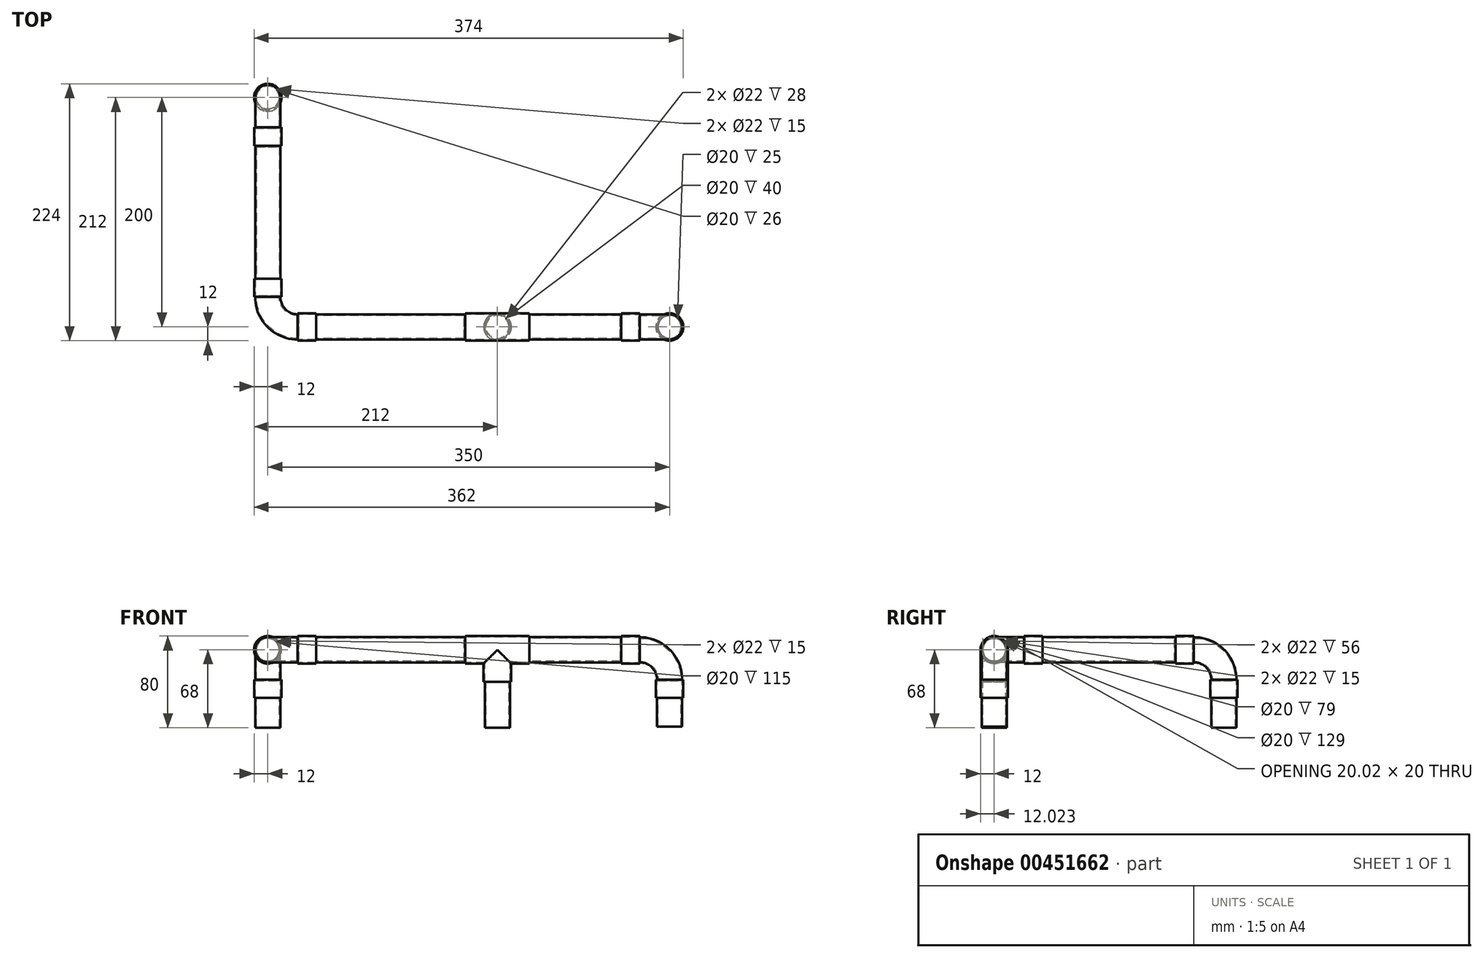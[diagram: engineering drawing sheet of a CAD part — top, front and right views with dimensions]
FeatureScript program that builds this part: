
annotation { "Feature Type Name" : "Feature", "Feature Type Description" : "" }
export const myFeature = defineFeature(function(context is Context, id is Id, definition is map)
    precondition{}
    {
        {
            var Q0;
            Q0=qCreatedBy(makeId("Top.planeOp"),FACE);
            var sketch = newSketch(context, id + "F0", { "sketchPlane" : qUnion([Q0])});
            skLineSegment(sketch, "E0", {"start": v(0, 26) * mm, "end": v(0, 26) * mm});
            skLineSegment(sketch, "E1", {"start": v(26, 0) * mm, "end": v(26, 0) * mm});
            skPoint(sketch, "E2.visualSharp", {"position": v(0, 0) * mm});
            skArc(sketch, "E2.filletArc", {"start": v(0, 26) * mm, "mid": v(7.62, 7.62) * mm, "end": v(26, 0) * mm});
            skPoint(sketch, "E3", {"position": v(0, 26) * mm});
            skPoint(sketch, "E4", {"position": v(26, 0) * mm});
            skSolve(sketch);
        }
        {
            var Q0;
            Q0=qCreatedBy(makeId("Front.planeOp"),FACE);
            var Q1;
            Q1=sQuery(id+"F0.wireOp",VERTEX,"E3");
            cPlane(context, id + "F1", {"entities" : qUnion([Q0, Q1]), "cplaneType" : CPlaneType.PLANE_POINT, "offset" : 25 * mm, "width" : 150 * mm, "height" : 150 * mm});
        }
        {
            var Q0;
            Q0=qCreatedBy(id+"F1.planeOp",FACE);
            var sketch = newSketch(context, id + "F2", { "sketchPlane" : qUnion([Q0])});
            skCircle(sketch, "E5", {"center": v(0, 0) * mm, "radius": 11 * mm});
            skSolve(sketch);
        }
        {
            var Q0;
            Q0=makeQuery(id+"F2.imprint","IMPRINT",FACE,{"disambiguationData":[TD([[makeQuery(id+"F2.imprint","IMPRINT",EDGE,{"derivedFrom":sQuery(id+"F2.wireOp",EDGE,"E5")}),1.0]])]});
            var Q1;
            Q1=sQuery(id+"F0.wireOp",EDGE,"E2.filletArc");
            sweep(context, id + "F3", {"profiles" : qUnion([Q0]), "path" : qUnion([Q1])});
        }
        {
            var Q0;
            Q0=makeQuery(id+"F3.opSweep","CAP_FACE",FACE,{"disambiguationData":[OSD([sQuery(id+"F0.wireOp",VERTEX,"E2.filletArc.start"),sQuery(id+"F2.wireOp",EDGE,"E5")])],"isStart":true});
            var sketch = newSketch(context, id + "F4", { "sketchPlane" : qUnion([Q0])});
            skCircle(sketch, "E6", {"center": v(0, 0) * mm, "radius": 12 * mm});
            skSolve(sketch);
        }
        {
            var Q0;
            Q0=makeQuery(id+"F4.imprint","IMPRINT",FACE,{"disambiguationData":[TD([[makeQuery(id+"F4.imprint","IMPRINT",EDGE,{"derivedFrom":sQuery(id+"F4.wireOp",EDGE,"E6")}),1.0]])]});
            var Q1;
            Q1=makeQuery(id+"F4.imprint","IMPRINT",FACE,{"disambiguationData":[TD([[makeQuery(id+"F4.imprint","IMPRINT",EDGE,{"derivedFrom":makeQuery(id+"F3.opSweep","CAP_EDGE",EDGE,{"disambiguationData":[OSD([sQuery(id+"F0.wireOp",VERTEX,"E2.filletArc.start"),sQuery(id+"F2.wireOp",EDGE,"E5")])],"isStart":true})}),-1.0]])]});
            extrude(context, id + "F5", {"entities" : qUnion([Q0, Q1]), "operationType" : NewBodyOperationType.ADD, "depth" : 16 * mm});
        }
        {
            var Q0;
            Q0=makeQuery(id+"F3.opSweep","CAP_FACE",FACE,{"disambiguationData":[OSD([sQuery(id+"F0.wireOp",VERTEX,"E2.filletArc.end"),sQuery(id+"F2.wireOp",EDGE,"E5")])],"isStart":false});
            var sketch = newSketch(context, id + "F6", { "sketchPlane" : qUnion([Q0])});
            skCircle(sketch, "E7", {"center": v(0, 0) * mm, "radius": 12 * mm});
            skSolve(sketch);
        }
        {
            var Q0;
            Q0=makeQuery(id+"F6.imprint","IMPRINT",FACE,{"disambiguationData":[TD([[makeQuery(id+"F6.imprint","IMPRINT",EDGE,{"derivedFrom":makeQuery(id+"F3.opSweep","CAP_EDGE",EDGE,{"disambiguationData":[OSD([sQuery(id+"F0.wireOp",VERTEX,"E2.filletArc.end"),sQuery(id+"F2.wireOp",EDGE,"E5")])],"isStart":false})}),1.0]])]});
            var Q1;
            Q1=makeQuery(id+"F6.imprint","IMPRINT",FACE,{"disambiguationData":[TD([[makeQuery(id+"F6.imprint","IMPRINT",EDGE,{"derivedFrom":sQuery(id+"F6.wireOp",EDGE,"E7")}),1.0]])]});
            extrude(context, id + "F7", {"entities" : qUnion([Q0, Q1]), "operationType" : NewBodyOperationType.ADD, "depth" : 16 * mm});
        }
        {
            var Q0;
            Q0=makeQuery(id+"F3.opSweep","SWEPT_BODY",BODY,{"disambiguationData":[OSD([sQuery(id+"F0.wireOp",EDGE,"E2.filletArc"),sQuery(id+"F2.wireOp",EDGE,"E5")])]});
            transform(context, id + "F8", {"entities" : qUnion([Q0]), "transformType" : TransformType.TRANSLATION_3D, "dx" : 350 * mm, "dy" : 0 * mm, "dz" : 0 * mm, "makeCopy" : true});
        }
        {
            var Q0;
            Q0=qCreatedBy(makeId("Top.planeOp"),FACE);
            var sketch = newSketch(context, id + "F9", { "sketchPlane" : qUnion([Q0])});
            skLineSegment(sketch, "E8.0", {"start": v(338, 42) * mm, "end": v(362, 42) * mm});
            skLineSegment(sketch, "E9", {"start": v(350, 42) * mm, "end": v(350, 75.2) * mm});
            skSolve(sketch);
        }
        {
            var Q0;
            Q0=makeQuery(id+"F8.opPattern","COPY",BODY,{"derivedFrom":makeQuery(id+"F3.opSweep","SWEPT_BODY",BODY,{"disambiguationData":[OSD([sQuery(id+"F0.wireOp",EDGE,"E2.filletArc"),sQuery(id+"F2.wireOp",EDGE,"E5")])]}),"instanceName":"1"});
            var Q1;
            Q1=sQuery(id+"F9.wireOp",EDGE,"E9");
            transform(context, id + "F10", {"entities" : qUnion([Q0]), "transformType" : TransformType.ROTATION, "transformAxis" : qUnion([Q1]), "angle" : 180 * degree, "makeCopy" : false});
        }
        {
            var Q0;
            Q0=qCreatedBy(makeId("Top.planeOp"),FACE);
            var sketch = newSketch(context, id + "F11", { "sketchPlane" : qUnion([Q0])});
            skLineSegment(sketch, "E10", {"start": v(0, 0) * mm, "end": v(0, 200) * mm});
            skLineSegment(sketch, "E11", {"start": v(0, 0) * mm, "end": v(200, 0) * mm});
            skLineSegment(sketch, "E12", {"start": v(200, 0) * mm, "end": v(350, 0) * mm});
            skLineSegment(sketch, "E13", {"start": v(350, 0) * mm, "end": v(350, 70) * mm});
            skSolve(sketch);
        }
        {
            var Q0;
            Q0=qCreatedBy(makeId("Front.planeOp"),FACE);
            var sketch = newSketch(context, id + "F12", { "sketchPlane" : qUnion([Q0])});
            skPoint(sketch, "E14.0", {"position": v(200, 0) * mm});
            skLineSegment(sketch, "E15", {"start": v(200, 0) * mm, "end": v(200, -70) * mm});
            skSolve(sketch);
        }
        {
            var Q0;
            Q0=qCreatedBy(makeId("Front.planeOp"),FACE);
            var Q1;
            Q1=sQuery(id+"F11.wireOp",VERTEX,"E10.end");
            cPlane(context, id + "F13", {"entities" : qUnion([Q0, Q1]), "cplaneType" : CPlaneType.PLANE_POINT, "offset" : 25 * mm, "width" : 150 * mm, "height" : 150 * mm});
        }
        {
            var Q0;
            Q0=qCreatedBy(id+"F13.planeOp",FACE);
            var sketch = newSketch(context, id + "F14", { "sketchPlane" : qUnion([Q0])});
            skLineSegment(sketch, "E16", {"start": v(0, 0) * mm, "end": v(0, -70) * mm});
            skSolve(sketch);
        }
        {
            var Q0;
            Q0=makeQuery(id+"F3.opSweep","SWEPT_BODY",BODY,{"disambiguationData":[OSD([sQuery(id+"F0.wireOp",EDGE,"E2.filletArc"),sQuery(id+"F2.wireOp",EDGE,"E5")])]});
            var Q1;
            Q1=sQuery(id+"F0.wireOp",VERTEX,"E2.visualSharp");
            var Q2;
            Q2=sQuery(id+"F14.wireOp",VERTEX,"E16.start");
            transform(context, id + "F15", {"entities" : qUnion([Q0]), "transformType" : TransformType.TRANSLATION_ENTITY, "oppositeDirectionEntity" : false, "transformLine" : qUnion([Q1, Q2]), "makeCopy" : true});
        }
        {
            var Q0;
            Q0=makeQuery(id+"F15.opPattern","COPY",BODY,{"derivedFrom":makeQuery(id+"F3.opSweep","SWEPT_BODY",BODY,{"disambiguationData":[OSD([sQuery(id+"F0.wireOp",EDGE,"E2.filletArc"),sQuery(id+"F2.wireOp",EDGE,"E5")])]}),"instanceName":"1"});
            var Q1;
            Q1=sQuery(id+"F14.wireOp",EDGE,"E16");
            transform(context, id + "F16", {"entities" : qUnion([Q0]), "transformType" : TransformType.ROTATION, "transformAxis" : qUnion([Q1]), "angle" : 90 * degree, "makeCopy" : false});
        }
        {
            var Q0;
            Q0=makeQuery(id+"F15.opPattern","COPY",BODY,{"derivedFrom":makeQuery(id+"F3.opSweep","SWEPT_BODY",BODY,{"disambiguationData":[OSD([sQuery(id+"F0.wireOp",EDGE,"E2.filletArc"),sQuery(id+"F2.wireOp",EDGE,"E5")])]}),"instanceName":"1"});
            var Q1;
            Q1=sQuery(id+"F11.wireOp",EDGE,"E10");
            transform(context, id + "F17", {"entities" : qUnion([Q0]), "transformType" : TransformType.ROTATION, "transformAxis" : qUnion([Q1]), "angle" : 90 * degree, "makeCopy" : false});
        }
        {
            var Q0;
            Q0=makeQuery(id+"F5.opExtrude","CAP_FACE",FACE,{"disambiguationData":[OSD([sQuery(id+"F4.wireOp",EDGE,"E6")])],"isStart":false});
            var sketch = newSketch(context, id + "F18", { "sketchPlane" : qUnion([Q0])});
            skCircle(sketch, "E17", {"center": v(0, 0) * mm, "radius": 11 * mm});
            skSolve(sketch);
        }
        {
            var Q0;
            Q0=makeQuery(id+"F18.imprint","IMPRINT",FACE,{"disambiguationData":[TD([[makeQuery(id+"F18.imprint","IMPRINT",EDGE,{"derivedFrom":sQuery(id+"F18.wireOp",EDGE,"E17")}),1.0]])]});
            extrude(context, id + "F19", {"entities" : qUnion([Q0]), "endBound" : BoundingType.UP_TO_NEXT, "depth" : 25 * mm});
        }
        {
            var Q0;
            Q0=qCreatedBy(makeId("Right.planeOp"),FACE);
            var Q1;
            Q1=sQuery(id+"F12.wireOp",VERTEX,"E14.0");
            cPlane(context, id + "F20", {"entities" : qUnion([Q0, Q1]), "cplaneType" : CPlaneType.PLANE_POINT, "offset" : 25 * mm, "width" : 150 * mm, "height" : 150 * mm});
        }
        {
            var Q0;
            Q0=qCreatedBy(id+"F20.planeOp",FACE);
            var sketch = newSketch(context, id + "F21", { "sketchPlane" : qUnion([Q0])});
            skCircle(sketch, "E18", {"center": v(0, 0) * mm, "radius": 12 * mm});
            skSolve(sketch);
        }
        {
            var Q0;
            Q0=makeQuery(id+"F21.imprint","IMPRINT",FACE,{"disambiguationData":[TD([[makeQuery(id+"F21.imprint","IMPRINT",EDGE,{"derivedFrom":sQuery(id+"F21.wireOp",EDGE,"E18")}),1.0]])]});
            extrude(context, id + "F22", {"entities" : qUnion([Q0]), "depth" : 56 * mm, "symmetric" : true});
        }
        {
            var Q0;
            Q0=qCreatedBy(makeId("Top.planeOp"),FACE);
            var sketch = newSketch(context, id + "F23", { "sketchPlane" : qUnion([Q0])});
            skPoint(sketch, "E19.0", {"position": v(200, 0) * mm});
            skCircle(sketch, "E20", {"center": v(200, 0) * mm, "radius": 12 * mm});
            skSolve(sketch);
        }
        {
            var Q0;
            Q0 = qSketchRegion(id + "F23", true);
            extrude(context, id + "F24", {"entities" : qUnion([Q0]), "operationType" : NewBodyOperationType.ADD, "oppositeDirection" : true, "depth" : 28 * mm});
        }
        {
            var Q0;
            Q0=makeQuery(id+"F7.opExtrude","CAP_FACE",FACE,{"disambiguationData":[OSD([sQuery(id+"F6.wireOp",EDGE,"E7")])],"isStart":false});
            var sketch = newSketch(context, id + "F25", { "sketchPlane" : qUnion([Q0])});
            skCircle(sketch, "E21", {"center": v(0, 0) * mm, "radius": 11 * mm});
            skSolve(sketch);
        }
        {
            var Q0;
            Q0=makeQuery(id+"F25.imprint","IMPRINT",FACE,{"disambiguationData":[TD([[makeQuery(id+"F25.imprint","IMPRINT",EDGE,{"derivedFrom":sQuery(id+"F25.wireOp",EDGE,"E21")}),1.0]])]});
            extrude(context, id + "F26", {"entities" : qUnion([Q0]), "endBound" : BoundingType.UP_TO_NEXT, "depth" : 25 * mm});
        }
        {
            var Q0;
            Q0=makeQuery(id+"F22.opExtrude","CAP_FACE",FACE,{"disambiguationData":[OSD([sQuery(id+"F21.wireOp",EDGE,"E18")])],"isStart":false});
            var sketch = newSketch(context, id + "F27", { "sketchPlane" : qUnion([Q0])});
            skCircle(sketch, "E22", {"center": v(0, 0) * mm, "radius": 11 * mm});
            skSolve(sketch);
        }
        {
            var Q0;
            Q0 = qSketchRegion(id + "F27", true);
            extrude(context, id + "F28", {"entities" : qUnion([Q0]), "endBound" : BoundingType.UP_TO_NEXT, "depth" : 25 * mm});
        }
        {
            var Q0;
            Q0=makeQuery(id+"F8.opPattern","COPY",BODY,{"derivedFrom":makeQuery(id+"F3.opSweep","SWEPT_BODY",BODY,{"disambiguationData":[OSD([sQuery(id+"F0.wireOp",EDGE,"E2.filletArc"),sQuery(id+"F2.wireOp",EDGE,"E5")])]}),"instanceName":"1"});
            var Q1;
            Q1=sQuery(id+"F11.wireOp",EDGE,"E12");
            transform(context, id + "F29", {"entities" : qUnion([Q0]), "transformType" : TransformType.ROTATION, "transformAxis" : qUnion([Q1]), "angle" : 270 * degree, "makeCopy" : false});
        }
        {
            var Q0;
            Q0=makeQuery(id+"F24.opExtrude","CAP_FACE",FACE,{"disambiguationData":[OSD([sQuery(id+"F23.wireOp",EDGE,"E20")])],"isStart":false});
            var sketch = newSketch(context, id + "F30", { "sketchPlane" : qUnion([Q0])});
            skCircle(sketch, "E23", {"center": v(200, 0) * mm, "radius": 11 * mm});
            skSolve(sketch);
        }
        {
            var Q0;
            Q0=makeQuery(id+"F30.imprint","IMPRINT",FACE,{"disambiguationData":[TD([[makeQuery(id+"F30.imprint","IMPRINT",EDGE,{"derivedFrom":sQuery(id+"F30.wireOp",EDGE,"E23")}),1.0]])]});
            extrude(context, id + "F31", {"entities" : qUnion([Q0]), "depth" : 40 * mm});
        }
        {
            var Q0;
            Q0=makeQuery(id+"F8.opPattern","COPY",FACE,{"derivedFrom":makeQuery(id+"F5.opExtrude","CAP_FACE",FACE,{"disambiguationData":[OSD([sQuery(id+"F4.wireOp",EDGE,"E6")])],"isStart":false}),"instanceName":"1"});
            var sketch = newSketch(context, id + "F32", { "sketchPlane" : qUnion([Q0])});
            skCircle(sketch, "E24", {"center": v(350, 0) * mm, "radius": 11 * mm});
            skSolve(sketch);
        }
        {
            var Q0;
            Q0=makeQuery(id+"F32.imprint","IMPRINT",FACE,{"disambiguationData":[TD([[makeQuery(id+"F32.imprint","IMPRINT",EDGE,{"derivedFrom":sQuery(id+"F32.wireOp",EDGE,"E24")}),1.0]])]});
            extrude(context, id + "F33", {"entities" : qUnion([Q0]), "depth" : 25 * mm});
        }
        {
            var Q0;
            Q0=makeQuery(id+"F15.opPattern","COPY",FACE,{"derivedFrom":makeQuery(id+"F5.opExtrude","CAP_FACE",FACE,{"disambiguationData":[OSD([sQuery(id+"F4.wireOp",EDGE,"E6")])],"isStart":false}),"instanceName":"1"});
            var sketch = newSketch(context, id + "F34", { "sketchPlane" : qUnion([Q0])});
            skCircle(sketch, "E25", {"center": v(0, -200) * mm, "radius": 11 * mm});
            skSolve(sketch);
        }
        {
            var Q0;
            Q0=makeQuery(id+"F34.imprint","IMPRINT",FACE,{"disambiguationData":[TD([[makeQuery(id+"F34.imprint","IMPRINT",EDGE,{"derivedFrom":sQuery(id+"F34.wireOp",EDGE,"E25")}),1.0]])]});
            extrude(context, id + "F35", {"entities" : qUnion([Q0]), "depth" : 26 * mm});
        }
        {
            var Q0;
            Q0=makeQuery(id+"F7.opExtrude","CAP_FACE",FACE,{"disambiguationData":[OSD([sQuery(id+"F6.wireOp",EDGE,"E7")])],"isStart":false});
            var Q1;
            Q1=makeQuery(id+"F5.opExtrude","CAP_FACE",FACE,{"disambiguationData":[OSD([sQuery(id+"F4.wireOp",EDGE,"E6")])],"isStart":false});
            shell(context, id + "F36", {"entities" : qUnion([Q0, Q1]), "thickness" : 1 * mm});
        }
        {
            var Q0;
            Q0=makeQuery(id+"F8.opPattern","COPY",FACE,{"derivedFrom":makeQuery(id+"F5.opExtrude","CAP_FACE",FACE,{"disambiguationData":[OSD([sQuery(id+"F4.wireOp",EDGE,"E6")])],"isStart":false}),"instanceName":"1"});
            var Q1;
            Q1=makeQuery(id+"F8.opPattern","COPY",FACE,{"derivedFrom":makeQuery(id+"F7.opExtrude","CAP_FACE",FACE,{"disambiguationData":[OSD([sQuery(id+"F6.wireOp",EDGE,"E7")])],"isStart":false}),"instanceName":"1"});
            shell(context, id + "F37", {"entities" : qUnion([Q0, Q1]), "thickness" : 1 * mm});
        }
        {
            var Q0;
            Q0=makeQuery(id+"F15.opPattern","COPY",FACE,{"derivedFrom":makeQuery(id+"F5.opExtrude","CAP_FACE",FACE,{"disambiguationData":[OSD([sQuery(id+"F4.wireOp",EDGE,"E6")])],"isStart":false}),"instanceName":"1"});
            var Q1;
            Q1=makeQuery(id+"F15.opPattern","COPY",FACE,{"derivedFrom":makeQuery(id+"F7.opExtrude","CAP_FACE",FACE,{"disambiguationData":[OSD([sQuery(id+"F6.wireOp",EDGE,"E7")])],"isStart":false}),"instanceName":"1"});
            shell(context, id + "F38", {"entities" : qUnion([Q0, Q1]), "thickness" : 1 * mm});
        }
        {
            var Q0;
            Q0=makeQuery(id+"F19.opExtrude","CAP_FACE",FACE,{"disambiguationData":[OSD([sQuery(id+"F6.wireOp",EDGE,"E7")])],"isStart":false});
            var Q1;
            Q1=makeQuery(id+"F19.opExtrude","CAP_FACE",FACE,{"disambiguationData":[OSD([sQuery(id+"F18.wireOp",EDGE,"E17")])],"isStart":true});
            shell(context, id + "F39", {"entities" : qUnion([Q0, Q1]), "thickness" : 1 * mm});
        }
        {
            var Q0;
            Q0=makeQuery(id+"F22.opExtrude","CAP_FACE",FACE,{"disambiguationData":[OSD([sQuery(id+"F21.wireOp",EDGE,"E18")])],"isStart":true});
            var Q1;
            Q1=makeQuery(id+"F22.opExtrude","CAP_FACE",FACE,{"disambiguationData":[OSD([sQuery(id+"F21.wireOp",EDGE,"E18")])],"isStart":false});
            var Q2;
            Q2=makeQuery(id+"F24.opExtrude","CAP_FACE",FACE,{"disambiguationData":[OSD([sQuery(id+"F23.wireOp",EDGE,"E20")])],"isStart":false});
            shell(context, id + "F40", {"entities" : qUnion([Q0, Q1, Q2]), "thickness" : 1 * mm});
        }
        {
            var Q0;
            Q0=makeQuery(id+"F26.opExtrude","CAP_FACE",FACE,{"disambiguationData":[OSD([sQuery(id+"F25.wireOp",EDGE,"E21")])],"isStart":true});
            var Q1;
            Q1=makeQuery(id+"F26.opExtrude","CAP_FACE",FACE,{"disambiguationData":[OSD([sQuery(id+"F21.wireOp",EDGE,"E18")])],"isStart":false});
            shell(context, id + "F41", {"entities" : qUnion([Q0, Q1]), "thickness" : 1 * mm});
        }
        {
            var Q0;
            Q0=makeQuery(id+"F28.opExtrude","CAP_FACE",FACE,{"disambiguationData":[OSD([sQuery(id+"F6.wireOp",EDGE,"E7")])],"isStart":false});
            var Q1;
            Q1=makeQuery(id+"F28.opExtrude","CAP_FACE",FACE,{"disambiguationData":[OSD([sQuery(id+"F27.wireOp",EDGE,"E22")])],"isStart":true});
            shell(context, id + "F42", {"entities" : qUnion([Q0, Q1]), "thickness" : 1 * mm});
        }
        {
            var Q0;
            Q0=makeQuery(id+"F31.opExtrude","CAP_FACE",FACE,{"disambiguationData":[OSD([sQuery(id+"F30.wireOp",EDGE,"E23")])],"isStart":false});
            var Q1;
            Q1=makeQuery(id+"F31.opExtrude","CAP_FACE",FACE,{"disambiguationData":[OSD([sQuery(id+"F30.wireOp",EDGE,"E23")])],"isStart":true});
            shell(context, id + "F43", {"entities" : qUnion([Q0, Q1]), "thickness" : 1 * mm});
        }
        {
            var Q0;
            Q0=makeQuery(id+"F33.opExtrude","CAP_FACE",FACE,{"disambiguationData":[OSD([sQuery(id+"F32.wireOp",EDGE,"E24")])],"isStart":false});
            var Q1;
            Q1=makeQuery(id+"F33.opExtrude","CAP_FACE",FACE,{"disambiguationData":[OSD([sQuery(id+"F32.wireOp",EDGE,"E24")])],"isStart":true});
            shell(context, id + "F44", {"entities" : qUnion([Q0, Q1]), "thickness" : 1 * mm});
        }
        {
            var Q0;
            Q0=makeQuery(id+"F35.opExtrude","CAP_FACE",FACE,{"disambiguationData":[OSD([sQuery(id+"F34.wireOp",EDGE,"E25")])],"isStart":false});
            var Q1;
            Q1=makeQuery(id+"F35.opExtrude","CAP_FACE",FACE,{"disambiguationData":[OSD([sQuery(id+"F34.wireOp",EDGE,"E25")])],"isStart":true});
            shell(context, id + "F45", {"entities" : qUnion([Q0, Q1]), "thickness" : 1 * mm});
        }
        {
            var Q0;
            Q0=makeQuery(id+"F22.opExtrude","SWEPT_BODY",BODY,{"disambiguationData":[OSD([sQuery(id+"F21.wireOp",EDGE,"E18")])]});
            transform(context, id + "F46", {"entities" : qUnion([Q0]), "transformType" : TransformType.TRANSLATION_3D, "dx" : 0 * mm, "dy" : 0 * mm, "dz" : 0 * mm, "makeCopy" : true});
        }
    });
